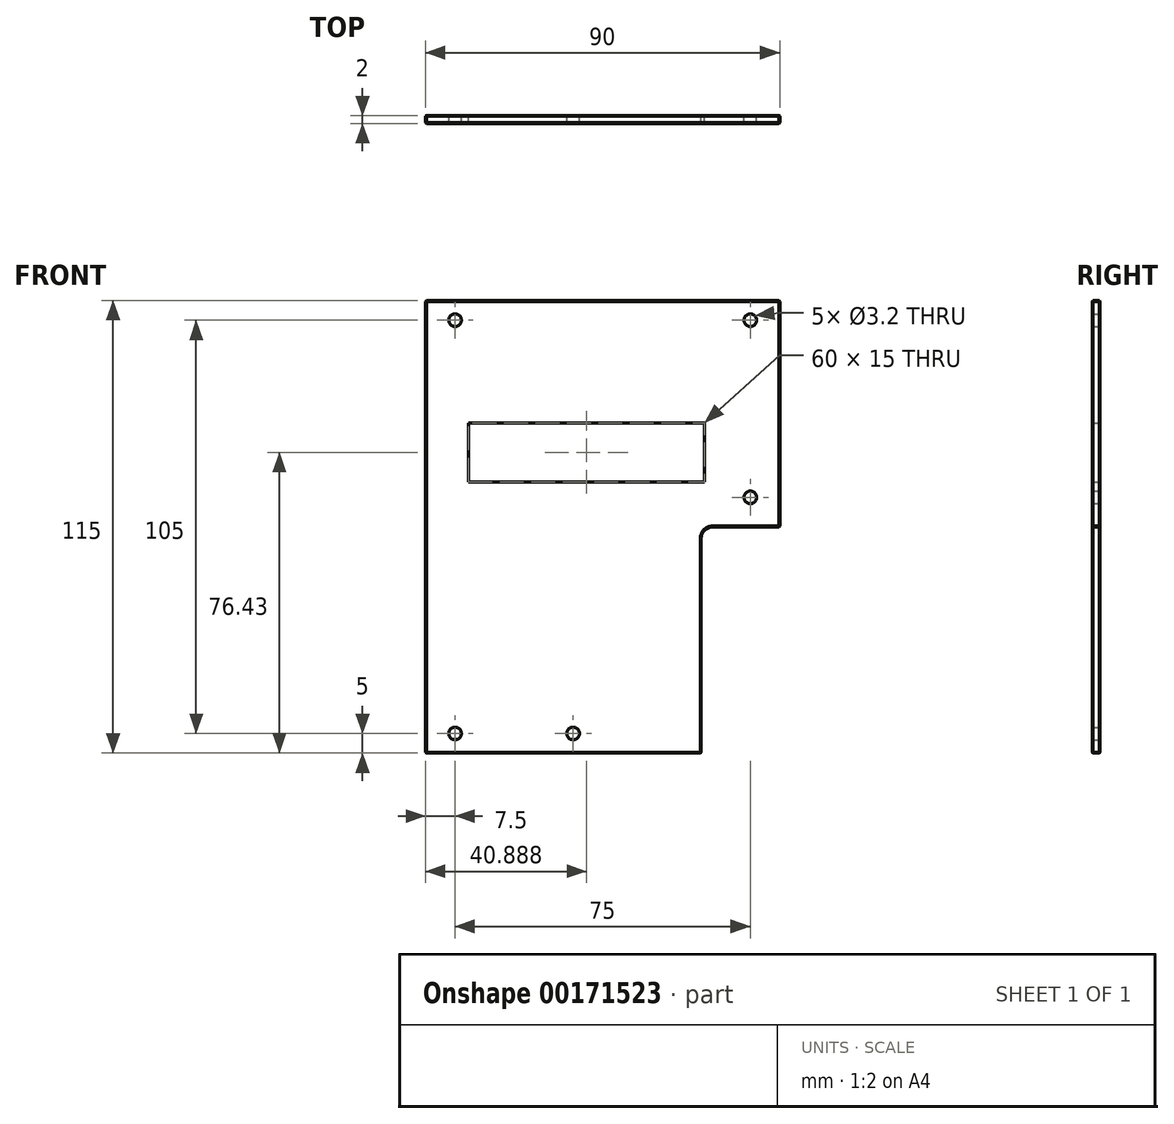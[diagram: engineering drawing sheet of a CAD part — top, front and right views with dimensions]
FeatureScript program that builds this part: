
annotation { "Feature Type Name" : "Feature", "Feature Type Description" : "" }
export const myFeature = defineFeature(function(context is Context, id is Id, definition is map)
    precondition{}
    {
        {
            var Q0;
            Q0=qCreatedBy(makeId("Front.planeOp"),FACE);
            var sketch = newSketch(context, id + "F0", { "sketchPlane" : qUnion([Q0])});
            skLineSegment(sketch, "E0.bottom", {"start": v(25, -57.5) * mm, "end": v(-45, -57.5) * mm});
            skLineSegment(sketch, "E0.top", {"start": v(45, 57.5) * mm, "end": v(-45, 57.5) * mm});
            skLineSegment(sketch, "E0.left", {"start": v(45, 0) * mm, "end": v(45, 57.5) * mm});
            skLineSegment(sketch, "E0.right", {"start": v(-45, -57.5) * mm, "end": v(-45, 57.5) * mm});
            skPoint(sketch, "E0.middle", {"position": v(0, 0) * mm});
            skCircle(sketch, "E1", {"center": v(-37.5, 52.5) * mm, "radius": 1.6 * mm});
            skCircle(sketch, "E2", {"center": v(37.5, 52.5) * mm, "radius": 1.6 * mm});
            skCircle(sketch, "E3", {"center": v(37.5, 7.5) * mm, "radius": 1.6 * mm});
            skCircle(sketch, "E4", {"center": v(-7.5, -52.5) * mm, "radius": 1.6 * mm});
            skLineSegment(sketch, "E5.top", {"start": v(45, 0) * mm, "end": v(25, 0) * mm});
            skLineSegment(sketch, "E5.right", {"start": v(25, -57.5) * mm, "end": v(25, 0) * mm});
            skPoint(sketch, "E6.orphan", {"position": v(45, -57.5) * mm});
            skLineSegment(sketch, "E7.bottom", {"start": v(-34.11, 11.43) * mm, "end": v(25.89, 11.43) * mm});
            skLineSegment(sketch, "E7.top", {"start": v(-34.11, 26.43) * mm, "end": v(25.89, 26.43) * mm});
            skLineSegment(sketch, "E7.left", {"start": v(-34.11, 11.43) * mm, "end": v(-34.11, 26.43) * mm});
            skLineSegment(sketch, "E7.right", {"start": v(25.89, 11.43) * mm, "end": v(25.89, 26.43) * mm});
            skCircle(sketch, "E8", {"center": v(-17.31, 22.5) * mm, "radius": 1.6 * mm});
            skCircle(sketch, "E9", {"center": v(7.69, 22.5) * mm, "radius": 1.6 * mm});
            skCircle(sketch, "E10", {"center": v(-37.5, -52.5) * mm, "radius": 1.6 * mm});
            skSolve(sketch);
        }
        {
            var Q0;
            Q0=makeQuery(id+"F0.imprint","IMPRINT",FACE,{"disambiguationData":[TD([[makeQuery(id+"F0.imprint","IMPRINT",EDGE,{"derivedFrom":sQuery(id+"F0.wireOp",EDGE,"E0.bottom")}),-1.0]])]});
            extrude(context, id + "F1", {"entities" : qUnion([Q0]), "depth" : 2 * mm});
        }
        {
            var Q0;
            Q0=makeQuery(id+"F1.opExtrude","SWEPT_EDGE",EDGE,{"disambiguationData":[OSD([sQuery(id+"F0.wireOp",EDGE,"E5.top"),sQuery(id+"F0.wireOp",EDGE,"E5.right")])]});
            fillet(context, id + "F2", {"entities" : qUnion([Q0]), "radius" : 3 * mm, "tangentPropagation" : true, "allowEdgeOverflow" : false});
        }
        {
            var Q0;
            Q0=makeQuery(id+"F1.opExtrude","CAP_EDGE",EDGE,{"disambiguationData":[OSD([sQuery(id+"F0.wireOp",EDGE,"E0.top")])],"isStart":false});
            var Q1;
            Q1=makeQuery(id+"F1.opExtrude","CAP_EDGE",EDGE,{"disambiguationData":[OSD([sQuery(id+"F0.wireOp",EDGE,"E0.top")])],"isStart":true});
            var Q2;
            Q2=makeQuery(id+"F1.opExtrude","SWEPT_EDGE",EDGE,{"disambiguationData":[OSD([sQuery(id+"F0.wireOp",EDGE,"E0.top"),sQuery(id+"F0.wireOp",EDGE,"E0.left")])]});
            var Q3;
            Q3=makeQuery(id+"F1.opExtrude","CAP_EDGE",EDGE,{"disambiguationData":[OSD([sQuery(id+"F0.wireOp",EDGE,"E0.left")])],"isStart":true});
            var Q4;
            Q4=makeQuery(id+"F1.opExtrude","CAP_EDGE",EDGE,{"disambiguationData":[OSD([sQuery(id+"F0.wireOp",EDGE,"E5.top")])],"isStart":false});
            var Q5;
            Q5=makeQuery(id+"F1.opExtrude","CAP_EDGE",EDGE,{"disambiguationData":[OSD([sQuery(id+"F0.wireOp",EDGE,"E0.left")])],"isStart":false});
            var Q6;
            Q6=makeQuery(id+"F1.opExtrude","CAP_EDGE",EDGE,{"disambiguationData":[OSD([sQuery(id+"F0.wireOp",EDGE,"E0.bottom")])],"isStart":false});
            var Q7;
            Q7=makeQuery(id+"F1.opExtrude","SWEPT_EDGE",EDGE,{"disambiguationData":[OSD([sQuery(id+"F0.wireOp",EDGE,"E0.left"),sQuery(id+"F0.wireOp",EDGE,"E5.top")])]});
            var Q8;
            Q8=makeQuery(id+"F1.opExtrude","CAP_EDGE",EDGE,{"disambiguationData":[OSD([sQuery(id+"F0.wireOp",EDGE,"E5.top")])],"isStart":true});
            var Q9;
            Q9=makeQuery(id+"F1.opExtrude","SWEPT_EDGE",EDGE,{"disambiguationData":[OSD([sQuery(id+"F0.wireOp",EDGE,"E0.bottom"),sQuery(id+"F0.wireOp",EDGE,"E5.right")])]});
            var Q10;
            Q10=makeQuery(id+"F1.opExtrude","CAP_EDGE",EDGE,{"disambiguationData":[OSD([sQuery(id+"F0.wireOp",EDGE,"E0.bottom")])],"isStart":true});
            var Q11;
            Q11=makeQuery(id+"F1.opExtrude","CAP_EDGE",EDGE,{"disambiguationData":[OSD([sQuery(id+"F0.wireOp",EDGE,"E0.right")])],"isStart":true});
            var Q12;
            Q12=makeQuery(id+"F1.opExtrude","CAP_EDGE",EDGE,{"disambiguationData":[OSD([sQuery(id+"F0.wireOp",EDGE,"E0.right")])],"isStart":false});
            var Q13;
            Q13=makeQuery(id+"F1.opExtrude","SWEPT_EDGE",EDGE,{"disambiguationData":[OSD([sQuery(id+"F0.wireOp",EDGE,"E0.top"),sQuery(id+"F0.wireOp",EDGE,"E0.right")])]});
            var Q14;
            Q14=makeQuery(id+"F1.opExtrude","SWEPT_EDGE",EDGE,{"disambiguationData":[OSD([sQuery(id+"F0.wireOp",EDGE,"E0.bottom"),sQuery(id+"F0.wireOp",EDGE,"E0.right")])]});
            chamfer(context, id + "F3", {"entities" : qUnion([Q0, Q1, Q2, Q3, Q4, Q5, Q6, Q7, Q8, Q9, Q10, Q11, Q12, Q13, Q14]), "width" : 0.2 * mm, "tangentPropagation" : true});
        }
    });
